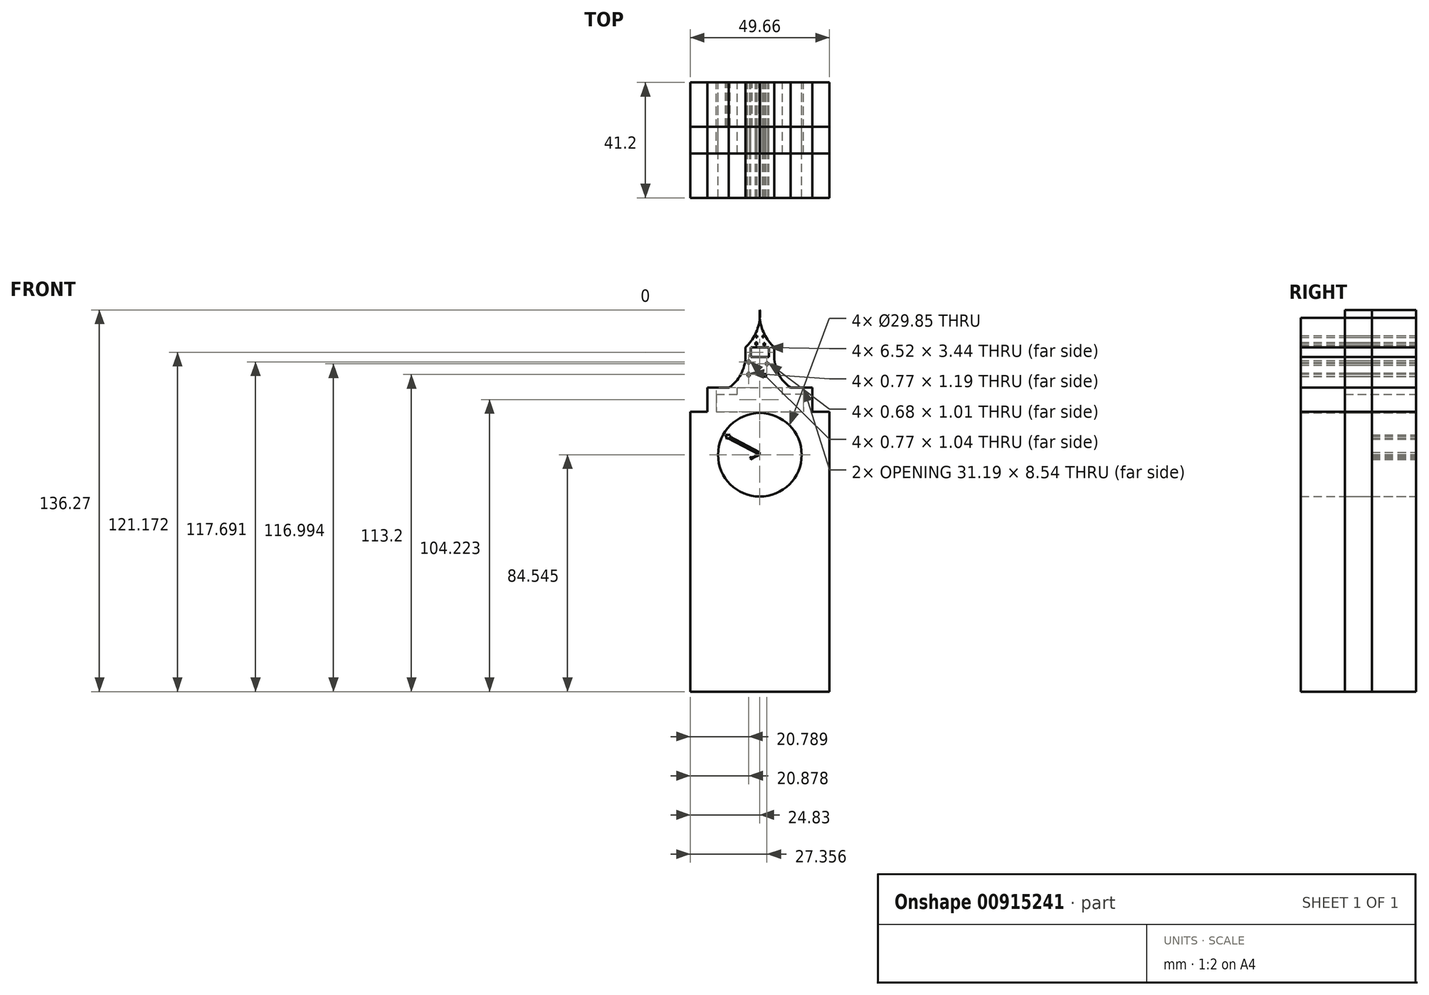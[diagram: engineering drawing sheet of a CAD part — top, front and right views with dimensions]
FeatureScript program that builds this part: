
annotation { "Feature Type Name" : "Feature", "Feature Type Description" : "" }
export const myFeature = defineFeature(function(context is Context, id is Id, definition is map)
    precondition{}
    {
        {
            var Q0;
            Q0=qCreatedBy(makeId("Front.planeOp"),FACE);
            var sketch = newSketch(context, id + "F0", { "sketchPlane" : qUnion([Q0])});
            skLineSegment(sketch, "E0", {"start": v(-24.83, -76.04) * mm, "end": v(-24.83, -7.77) * mm});
            skLineSegment(sketch, "E1", {"start": v(-24.83, -7.77) * mm, "end": v(0, -7.77) * mm});
            skLineSegment(sketch, "E2.MirrorCS", {"start": v(24.83, -76.04) * mm, "end": v(24.83, -7.77) * mm});
            skLineSegment(sketch, "E3.MirrorCS", {"start": v(24.83, -7.77) * mm, "end": v(0, -7.77) * mm});
            skLineSegment(sketch, "E4", {"start": v(-24.83, -7.77) * mm, "end": v(-24.83, 23.76) * mm});
            skLineSegment(sketch, "E5.MirrorCS", {"start": v(24.83, -7.77) * mm, "end": v(24.83, 23.76) * mm});
            skCircle(sketch, "E6", {"center": v(0, 8.36) * mm, "radius": 14.92 * mm});
            skLineSegment(sketch, "E7", {"start": v(-24.83, 23.76) * mm, "end": v(24.83, 23.76) * mm});
            skLineSegment(sketch, "E8", {"start": v(-18.75, 23.76) * mm, "end": v(-18.75, 29.91) * mm});
            skLineSegment(sketch, "E9", {"start": v(-18.75, 29.91) * mm, "end": v(0, 29.91) * mm});
            skLineSegment(sketch, "E10", {"start": v(-15.6, 29.91) * mm, "end": v(-15.6, 23.76) * mm});
            skLineSegment(sketch, "E11", {"start": v(-11.56, 29.91) * mm, "end": v(-11.56, 23.76) * mm});
            skLineSegment(sketch, "E12", {"start": v(-8.12, 29.91) * mm, "end": v(-8.12, 23.76) * mm});
            skLineSegment(sketch, "E13", {"start": v(-4.8, 29.91) * mm, "end": v(-4.8, 23.76) * mm});
            skLineSegment(sketch, "E14", {"start": v(-1.36, 29.91) * mm, "end": v(-1.36, 23.76) * mm});
            skLineSegment(sketch, "E15.MirrorCS", {"start": v(18.75, 29.91) * mm, "end": v(0, 29.91) * mm});
            skLineSegment(sketch, "E16.MirrorCS", {"start": v(18.75, 23.76) * mm, "end": v(18.75, 29.91) * mm});
            skLineSegment(sketch, "E17.MirrorCS", {"start": v(15.6, 29.91) * mm, "end": v(15.6, 23.76) * mm});
            skLineSegment(sketch, "E18.MirrorCS", {"start": v(11.56, 29.91) * mm, "end": v(11.56, 23.76) * mm});
            skLineSegment(sketch, "E19.MirrorCS", {"start": v(8.12, 29.91) * mm, "end": v(8.12, 23.76) * mm});
            skLineSegment(sketch, "E20.MirrorCS", {"start": v(4.8, 29.91) * mm, "end": v(4.8, 23.76) * mm});
            skLineSegment(sketch, "E21.MirrorCS", {"start": v(1.36, 29.91) * mm, "end": v(1.36, 23.76) * mm});
            skArc(sketch, "E22", {"start": v(-11.05, 32.3) * mm, "mid": v(-6.78, 37.07) * mm, "end": v(-5.16, 43.26) * mm});
            skLineSegment(sketch, "E23", {"start": v(-5.16, 43.26) * mm, "end": v(5.16, 43.26) * mm});
            skLineSegment(sketch, "E24", {"start": v(-3.26, 43.26) * mm, "end": v(-3.26, 46.7) * mm});
            skLineSegment(sketch, "E25", {"start": v(-5.16, 43.26) * mm, "end": v(-5.16, 46.7) * mm});
            skLineSegment(sketch, "E26", {"start": v(-5.16, 46.7) * mm, "end": v(0, 46.7) * mm});
            skLineSegment(sketch, "E27", {"start": v(-1.25, 46.7) * mm, "end": v(-1.25, 43.26) * mm});
            skLineSegment(sketch, "E28.MirrorCS", {"start": v(5.16, 46.7) * mm, "end": v(0, 46.7) * mm});
            skLineSegment(sketch, "E29.MirrorCS", {"start": v(1.25, 46.7) * mm, "end": v(1.25, 43.26) * mm});
            skLineSegment(sketch, "E30.MirrorCS", {"start": v(3.26, 43.26) * mm, "end": v(3.26, 46.7) * mm});
            skLineSegment(sketch, "E31.MirrorCS", {"start": v(5.16, 43.26) * mm, "end": v(5.16, 46.7) * mm});
            skArc(sketch, "E32", {"start": v(-5.16, 46.7) * mm, "mid": v(-1.02, 52.8) * mm, "end": v(0, 60.08) * mm});
            skArc(sketch, "E33.MirrorCS", {"start": v(5.16, 46.7) * mm, "mid": v(1.02, 52.8) * mm, "end": v(0, 60.08) * mm});
            skLineSegment(sketch, "E34", {"start": v(-5.16, 46.7) * mm, "end": v(-5.16, 50.35) * mm});
            skLineSegment(sketch, "E35", {"start": v(5.16, 46.7) * mm, "end": v(5.16, 51.06) * mm});
            skLineSegment(sketch, "E36", {"start": v(-18.75, 29.91) * mm, "end": v(-18.75, 32.3) * mm});
            skLineSegment(sketch, "E37", {"start": v(-18.75, 32.3) * mm, "end": v(0, 32.3) * mm});
            skLineSegment(sketch, "E38", {"start": v(-15.6, 32.3) * mm, "end": v(-15.6, 29.91) * mm});
            skLineSegment(sketch, "E39", {"start": v(-11.56, 29.91) * mm, "end": v(-11.56, 31.97) * mm});
            skLineSegment(sketch, "E40", {"start": v(-11.56, 31.97) * mm, "end": v(-11.56, 32.3) * mm});
            skLineSegment(sketch, "E41", {"start": v(-8.12, 29.91) * mm, "end": v(-8.12, 32.3) * mm});
            skLineSegment(sketch, "E42", {"start": v(-4.8, 29.91) * mm, "end": v(-4.8, 32.3) * mm});
            skLineSegment(sketch, "E43", {"start": v(-1.36, 29.91) * mm, "end": v(-1.36, 32.3) * mm});
            skLineSegment(sketch, "E44.MirrorCS", {"start": v(1.36, 29.91) * mm, "end": v(1.36, 32.3) * mm});
            skLineSegment(sketch, "E45.MirrorCS", {"start": v(4.8, 29.91) * mm, "end": v(4.8, 32.3) * mm});
            skLineSegment(sketch, "E46.MirrorCS", {"start": v(8.12, 29.91) * mm, "end": v(8.12, 32.3) * mm});
            skLineSegment(sketch, "E47.MirrorCS", {"start": v(11.56, 29.91) * mm, "end": v(11.56, 31.97) * mm});
            skLineSegment(sketch, "E48.MirrorCS", {"start": v(15.6, 32.3) * mm, "end": v(15.6, 29.91) * mm});
            skLineSegment(sketch, "E49.MirrorCS", {"start": v(18.75, 29.91) * mm, "end": v(18.75, 32.3) * mm});
            skLineSegment(sketch, "E50.MirrorCS", {"start": v(18.75, 32.3) * mm, "end": v(0, 32.3) * mm});
            skLineSegment(sketch, "E51.bottom", {"start": v(-4.43, 42.02) * mm, "end": v(-3.66, 42.02) * mm});
            skLineSegment(sketch, "E51.top", {"start": v(-4.43, 40.98) * mm, "end": v(-3.66, 40.98) * mm});
            skLineSegment(sketch, "E51.left", {"start": v(-4.43, 42.02) * mm, "end": v(-4.43, 40.98) * mm});
            skLineSegment(sketch, "E51.right", {"start": v(-3.66, 42.02) * mm, "end": v(-3.66, 40.98) * mm});
            skLineSegment(sketch, "E52.bottom", {"start": v(2.19, 41.3) * mm, "end": v(2.87, 41.3) * mm});
            skLineSegment(sketch, "E52.top", {"start": v(2.19, 40.3) * mm, "end": v(2.87, 40.3) * mm});
            skLineSegment(sketch, "E52.left", {"start": v(2.19, 41.3) * mm, "end": v(2.19, 40.3) * mm});
            skLineSegment(sketch, "E52.right", {"start": v(2.87, 41.3) * mm, "end": v(2.87, 40.3) * mm});
            skLineSegment(sketch, "E53.bottom", {"start": v(-4.34, 37.6) * mm, "end": v(-3.57, 37.6) * mm});
            skLineSegment(sketch, "E53.top", {"start": v(-4.34, 36.42) * mm, "end": v(-3.57, 36.42) * mm});
            skLineSegment(sketch, "E53.left", {"start": v(-4.34, 37.6) * mm, "end": v(-4.34, 36.42) * mm});
            skLineSegment(sketch, "E53.right", {"start": v(-3.57, 37.6) * mm, "end": v(-3.57, 36.42) * mm});
            skLineSegment(sketch, "E54.bottom", {"start": v(1.33, 37.22) * mm, "end": v(2.21, 37.22) * mm});
            skLineSegment(sketch, "E54.top", {"start": v(1.33, 36.27) * mm, "end": v(2.21, 36.27) * mm});
            skLineSegment(sketch, "E54.left", {"start": v(1.33, 37.22) * mm, "end": v(1.33, 36.27) * mm});
            skLineSegment(sketch, "E54.right", {"start": v(2.21, 37.22) * mm, "end": v(2.21, 36.27) * mm});
            skLineSegment(sketch, "E55.bottom", {"start": v(-1.5, 50.91) * mm, "end": v(-0.99, 50.91) * mm});
            skLineSegment(sketch, "E55.top", {"start": v(-1.5, 50.26) * mm, "end": v(-0.99, 50.26) * mm});
            skLineSegment(sketch, "E55.left", {"start": v(-1.5, 50.91) * mm, "end": v(-1.5, 50.26) * mm});
            skLineSegment(sketch, "E55.right", {"start": v(-0.99, 50.91) * mm, "end": v(-0.99, 50.26) * mm});
            skLineSegment(sketch, "E56.bottom", {"start": v(0.94, 50.88) * mm, "end": v(1.36, 50.88) * mm});
            skLineSegment(sketch, "E56.top", {"start": v(0.94, 50.26) * mm, "end": v(1.36, 50.26) * mm});
            skLineSegment(sketch, "E56.left", {"start": v(0.94, 50.88) * mm, "end": v(0.94, 50.26) * mm});
            skLineSegment(sketch, "E56.right", {"start": v(1.36, 50.88) * mm, "end": v(1.36, 50.26) * mm});
            skLineSegment(sketch, "E57.bottom", {"start": v(-1.64, 48.48) * mm, "end": v(-0.99, 48.48) * mm});
            skLineSegment(sketch, "E57.top", {"start": v(-1.64, 47.65) * mm, "end": v(-0.99, 47.65) * mm});
            skLineSegment(sketch, "E57.left", {"start": v(-1.64, 48.48) * mm, "end": v(-1.64, 47.65) * mm});
            skLineSegment(sketch, "E57.right", {"start": v(-0.99, 48.48) * mm, "end": v(-0.99, 47.65) * mm});
            skLineSegment(sketch, "E58.bottom", {"start": v(1.36, 48.25) * mm, "end": v(1.83, 48.25) * mm});
            skLineSegment(sketch, "E58.top", {"start": v(1.36, 47.33) * mm, "end": v(1.83, 47.33) * mm});
            skLineSegment(sketch, "E58.left", {"start": v(1.36, 48.25) * mm, "end": v(1.36, 47.33) * mm});
            skLineSegment(sketch, "E58.right", {"start": v(1.83, 48.25) * mm, "end": v(1.83, 47.33) * mm});
            skLineSegment(sketch, "E59", {"start": v(-24.83, -70.53) * mm, "end": v(24.83, -70.53) * mm});
            skLineSegment(sketch, "E60", {"start": v(-24.83, -51.07) * mm, "end": v(24.83, -51.07) * mm});
            skLineSegment(sketch, "E61", {"start": v(-24.83, -36.26) * mm, "end": v(24.83, -36.26) * mm});
            skLineSegment(sketch, "E62", {"start": v(-24.83, -20.33) * mm, "end": v(24.83, -20.33) * mm});
            skLineSegment(sketch, "E63", {"start": v(-24.83, -76.04) * mm, "end": v(-24.83, -76.2) * mm});
            skLineSegment(sketch, "E64", {"start": v(24.83, -76.04) * mm, "end": v(24.83, -76.19) * mm});
            skLineSegment(sketch, "E65", {"start": v(24.83, -76.19) * mm, "end": v(24.83, -76.2) * mm});
            skLineSegment(sketch, "E66", {"start": v(24.83, -76.2) * mm, "end": v(24.83, -76.2) * mm});
            skLineSegment(sketch, "E67", {"start": v(-24.83, -76.2) * mm, "end": v(-24.83, -76.2) * mm});
            skLineSegment(sketch, "E68", {"start": v(-24.83, -76.2) * mm, "end": v(24.83, -76.19) * mm});
            skArc(sketch, "E69.trimOffspring", {"start": v(11.05, 32.3) * mm, "mid": v(6.78, 37.07) * mm, "end": v(5.16, 43.26) * mm});
            skPoint(sketch, "E70.MirrorCS.start.orphan", {"position": v(18.75, 29.91) * mm});
            skLineSegment(sketch, "E71", {"start": v(11.56, 31.97) * mm, "end": v(11.56, 32.3) * mm});
            skLineSegment(sketch, "E72", {"start": v(0, 8.36) * mm, "end": v(-11.46, 14.36) * mm});
            skLineSegment(sketch, "E73", {"start": v(0, 9.22) * mm, "end": v(-10.86, 14.91) * mm});
            skLineSegment(sketch, "E74", {"start": v(-10.86, 14.91) * mm, "end": v(-10.55, 15.5) * mm});
            skLineSegment(sketch, "E75", {"start": v(-10.55, 15.5) * mm, "end": v(-12.22, 15.5) * mm});
            skLineSegment(sketch, "E76", {"start": v(-12.22, 15.5) * mm, "end": v(-11.78, 13.98) * mm});
            skLineSegment(sketch, "E77", {"start": v(-11.78, 13.98) * mm, "end": v(-11.46, 14.36) * mm});
            skLineSegment(sketch, "E78", {"start": v(0, 8.36) * mm, "end": v(0, 9.22) * mm});
            skLineSegment(sketch, "E79", {"start": v(0, 8.36) * mm, "end": v(-2.76, 7.1) * mm});
            skLineSegment(sketch, "E80", {"start": v(-2.76, 7.1) * mm, "end": v(-3.1, 7.86) * mm});
            skLineSegment(sketch, "E81", {"start": v(-3.1, 7.86) * mm, "end": v(-3.5, 7.12) * mm});
            skLineSegment(sketch, "E82", {"start": v(-3.5, 7.12) * mm, "end": v(-2.76, 6.73) * mm});
            skLineSegment(sketch, "E83", {"start": v(-2.76, 6.73) * mm, "end": v(-2.76, 7.1) * mm});
            skLineSegment(sketch, "E84", {"start": v(-2.87, 7.36) * mm, "end": v(-0.29, 8.5) * mm});
            skSolve(sketch);
        }
        {
            var Q0;
            Q0 = qSketchRegion(id + "F0", true);
            var Q1;
            {var subQ0=sQuery(id+"F0.wireOp",EDGE,"E10");Q1=makeQuery(id+"F0.imprint","IMPRINT",FACE,{"disambiguationData":[TD([[makeQuery(id+"F0.imprint","IMPRINT",EDGE,{"derivedFrom":subQ0}),1.0]])]});}
            var Q2;
            {var subQ0=sQuery(id+"F0.wireOp",EDGE,"E11");Q2=makeQuery(id+"F0.imprint","IMPRINT",FACE,{"disambiguationData":[TD([[makeQuery(id+"F0.imprint","IMPRINT",EDGE,{"derivedFrom":subQ0}),1.0]])]});}
            var Q3;
            {var subQ0=sQuery(id+"F0.wireOp",EDGE,"E12");Q3=makeQuery(id+"F0.imprint","IMPRINT",FACE,{"disambiguationData":[TD([[makeQuery(id+"F0.imprint","IMPRINT",EDGE,{"derivedFrom":subQ0}),1.0]])]});}
            var Q4;
            {var subQ0=sQuery(id+"F0.wireOp",EDGE,"E13");Q4=makeQuery(id+"F0.imprint","IMPRINT",FACE,{"disambiguationData":[TD([[makeQuery(id+"F0.imprint","IMPRINT",EDGE,{"derivedFrom":subQ0}),1.0]])]});}
            var Q5;
            {var subQ4=sQuery(id+"F0.wireOp",EDGE,"E14");Q5=makeQuery(id+"F0.imprint","IMPRINT",FACE,{"disambiguationData":[TD([[makeQuery(id+"F0.imprint","IMPRINT",EDGE,{"derivedFrom":subQ4}),1.0]])]});}
            var Q6;
            {var subQ0=sQuery(id+"F0.wireOp",EDGE,"E20.MirrorCS");Q6=makeQuery(id+"F0.imprint","IMPRINT",FACE,{"disambiguationData":[TD([[makeQuery(id+"F0.imprint","IMPRINT",EDGE,{"derivedFrom":subQ0}),-1.0]])]});}
            var Q7;
            {var subQ0=sQuery(id+"F0.wireOp",EDGE,"E19.MirrorCS");Q7=makeQuery(id+"F0.imprint","IMPRINT",FACE,{"disambiguationData":[TD([[makeQuery(id+"F0.imprint","IMPRINT",EDGE,{"derivedFrom":subQ0}),-1.0]])]});}
            var Q8;
            {var subQ0=sQuery(id+"F0.wireOp",EDGE,"E18.MirrorCS");Q8=makeQuery(id+"F0.imprint","IMPRINT",FACE,{"disambiguationData":[TD([[makeQuery(id+"F0.imprint","IMPRINT",EDGE,{"derivedFrom":subQ0}),-1.0]])]});}
            var Q9;
            {var subQ0=sQuery(id+"F0.wireOp",EDGE,"E17.MirrorCS");Q9=makeQuery(id+"F0.imprint","IMPRINT",FACE,{"disambiguationData":[TD([[makeQuery(id+"F0.imprint","IMPRINT",EDGE,{"derivedFrom":subQ0}),-1.0]])]});}
            var Q10;
            {var subQ0=sQuery(id+"F0.wireOp",EDGE,"E43");Q10=makeQuery(id+"F0.imprint","IMPRINT",FACE,{"disambiguationData":[TD([[makeQuery(id+"F0.imprint","IMPRINT",EDGE,{"derivedFrom":subQ0}),-1.0]])]});}
            var Q11;
            {var subQ0=sQuery(id+"F0.wireOp",EDGE,"E42");Q11=makeQuery(id+"F0.imprint","IMPRINT",FACE,{"disambiguationData":[TD([[makeQuery(id+"F0.imprint","IMPRINT",EDGE,{"derivedFrom":subQ0}),-1.0]])]});}
            var Q12;
            {var subQ0=sQuery(id+"F0.wireOp",EDGE,"E41");Q12=makeQuery(id+"F0.imprint","IMPRINT",FACE,{"disambiguationData":[TD([[makeQuery(id+"F0.imprint","IMPRINT",EDGE,{"derivedFrom":subQ0}),-1.0]])]});}
            var Q13;
            {var subQ2=sQuery(id+"F0.wireOp",EDGE,"E45.MirrorCS");Q13=makeQuery(id+"F0.imprint","IMPRINT",FACE,{"disambiguationData":[TD([[makeQuery(id+"F0.imprint","IMPRINT",EDGE,{"derivedFrom":subQ2}),-1.0]])]});}
            var Q14;
            {var subQ2=sQuery(id+"F0.wireOp",EDGE,"E44.MirrorCS");Q14=makeQuery(id+"F0.imprint","IMPRINT",FACE,{"disambiguationData":[TD([[makeQuery(id+"F0.imprint","IMPRINT",EDGE,{"derivedFrom":subQ2}),-1.0]])]});}
            var Q15;
            Q15=makeQuery(id+"F0.imprint","IMPRINT",FACE,{"disambiguationData":[TD([[makeQuery(id+"F0.imprint","IMPRINT",EDGE,{"derivedFrom":sQuery(id+"F0.wireOp",EDGE,"E73")}),1.0]])]});
            var Q16;
            {var subQ0=sQuery(id+"F0.wireOp",EDGE,"E79");Q16=makeQuery(id+"F0.imprint","IMPRINT",FACE,{"disambiguationData":[TD([[makeQuery(id+"F0.imprint","IMPRINT",EDGE,{"derivedFrom":subQ0}),-1.0]])]});}
            var Q17;
            {var subQ0=sQuery(id+"F0.wireOp",EDGE,"E81");Q17=makeQuery(id+"F0.imprint","IMPRINT",FACE,{"disambiguationData":[TD([[makeQuery(id+"F0.imprint","IMPRINT",EDGE,{"derivedFrom":subQ0}),1.0]])]});}
            extrude(context, id + "F1", {"entities" : qUnion([Q0, Q1, Q2, Q3, Q4, Q5, Q6, Q7, Q8, Q9, Q10, Q11, Q12, Q13, Q14, Q15, Q16, Q17]), "depth" : 15.8 * mm, "offsetDistance" : 25.4 * mm});
        }
        {
            var Q0;
            Q0 = qSketchRegion(id + "F0", true);
            extrude(context, id + "F2", {"entities" : qUnion([Q0]), "depth" : 25.4 * mm, "offsetDistance" : 25.4 * mm});
        }
        {
            var Q0;
            Q0 = qSketchRegion(id + "F0", true);
            var Q1;
            Q1=makeQuery(id+"F1.opExtrude","CAP_FACE",FACE,{"disambiguationData":[OSD([sQuery(id+"F0.wireOp",EDGE,"E0"),sQuery(id+"F0.wireOp",EDGE,"E2.MirrorCS"),sQuery(id+"F0.wireOp",EDGE,"E4"),sQuery(id+"F0.wireOp",EDGE,"E5.MirrorCS"),sQuery(id+"F0.wireOp",EDGE,"E6"),sQuery(id+"F0.wireOp",EDGE,"E7"),sQuery(id+"F0.wireOp",EDGE,"E8"),sQuery(id+"F0.wireOp",EDGE,"E9"),sQuery(id+"F0.wireOp",EDGE,"E10"),sQuery(id+"F0.wireOp",EDGE,"E15.MirrorCS"),sQuery(id+"F0.wireOp",EDGE,"E16.MirrorCS"),sQuery(id+"F0.wireOp",EDGE,"E17.MirrorCS"),sQuery(id+"F0.wireOp",EDGE,"E22"),sQuery(id+"F0.wireOp",EDGE,"E70.MirrorCS"),sQuery(id+"F0.wireOp",EDGE,"E23"),sQuery(id+"F0.wireOp",EDGE,"E24"),sQuery(id+"F0.wireOp",EDGE,"E25"),sQuery(id+"F0.wireOp",EDGE,"E26"),sQuery(id+"F0.wireOp",EDGE,"E28.MirrorCS"),sQuery(id+"F0.wireOp",EDGE,"E30.MirrorCS"),sQuery(id+"F0.wireOp",EDGE,"E31.MirrorCS"),sQuery(id+"F0.wireOp",EDGE,"E32"),sQuery(id+"F0.wireOp",EDGE,"E33.MirrorCS"),sQuery(id+"F0.wireOp",EDGE,"E36"),sQuery(id+"F0.wireOp",EDGE,"E37"),sQuery(id+"F0.wireOp",EDGE,"E38"),sQuery(id+"F0.wireOp",EDGE,"E39"),sQuery(id+"F0.wireOp",EDGE,"E41"),sQuery(id+"F0.wireOp",EDGE,"E46.MirrorCS"),sQuery(id+"F0.wireOp",EDGE,"E47.MirrorCS"),sQuery(id+"F0.wireOp",EDGE,"E48.MirrorCS"),sQuery(id+"F0.wireOp",EDGE,"E49.MirrorCS"),sQuery(id+"F0.wireOp",EDGE,"E50.MirrorCS"),sQuery(id+"F0.wireOp",EDGE,"E51.bottom"),sQuery(id+"F0.wireOp",EDGE,"E51.top"),sQuery(id+"F0.wireOp",EDGE,"E51.left"),sQuery(id+"F0.wireOp",EDGE,"E51.right"),sQuery(id+"F0.wireOp",EDGE,"E52.bottom"),sQuery(id+"F0.wireOp",EDGE,"E52.top"),sQuery(id+"F0.wireOp",EDGE,"E52.left"),sQuery(id+"F0.wireOp",EDGE,"E52.right"),sQuery(id+"F0.wireOp",EDGE,"E53.bottom"),sQuery(id+"F0.wireOp",EDGE,"E53.top"),sQuery(id+"F0.wireOp",EDGE,"E53.left"),sQuery(id+"F0.wireOp",EDGE,"E53.right"),sQuery(id+"F0.wireOp",EDGE,"E54.bottom"),sQuery(id+"F0.wireOp",EDGE,"E54.top"),sQuery(id+"F0.wireOp",EDGE,"E54.left"),sQuery(id+"F0.wireOp",EDGE,"E54.right"),sQuery(id+"F0.wireOp",EDGE,"E55.bottom"),sQuery(id+"F0.wireOp",EDGE,"E55.top"),sQuery(id+"F0.wireOp",EDGE,"E55.left"),sQuery(id+"F0.wireOp",EDGE,"E55.right"),sQuery(id+"F0.wireOp",EDGE,"E56.bottom"),sQuery(id+"F0.wireOp",EDGE,"E56.top"),sQuery(id+"F0.wireOp",EDGE,"E56.left"),sQuery(id+"F0.wireOp",EDGE,"E56.right"),sQuery(id+"F0.wireOp",EDGE,"E57.bottom"),sQuery(id+"F0.wireOp",EDGE,"E57.top"),sQuery(id+"F0.wireOp",EDGE,"E57.left"),sQuery(id+"F0.wireOp",EDGE,"E57.right"),sQuery(id+"F0.wireOp",EDGE,"E58.bottom"),sQuery(id+"F0.wireOp",EDGE,"E58.top"),sQuery(id+"F0.wireOp",EDGE,"E58.left"),sQuery(id+"F0.wireOp",EDGE,"E58.right"),sQuery(id+"F0.wireOp",EDGE,"E63"),sQuery(id+"F0.wireOp",EDGE,"E64"),sQuery(id+"F0.wireOp",EDGE,"E68")])],"isStart":false});
            extrude(context, id + "F3", {"entities" : qUnion([Q0, Q1]), "depth" : 25.4 * mm, "offsetDistance" : 25.4 * mm});
        }
    });
